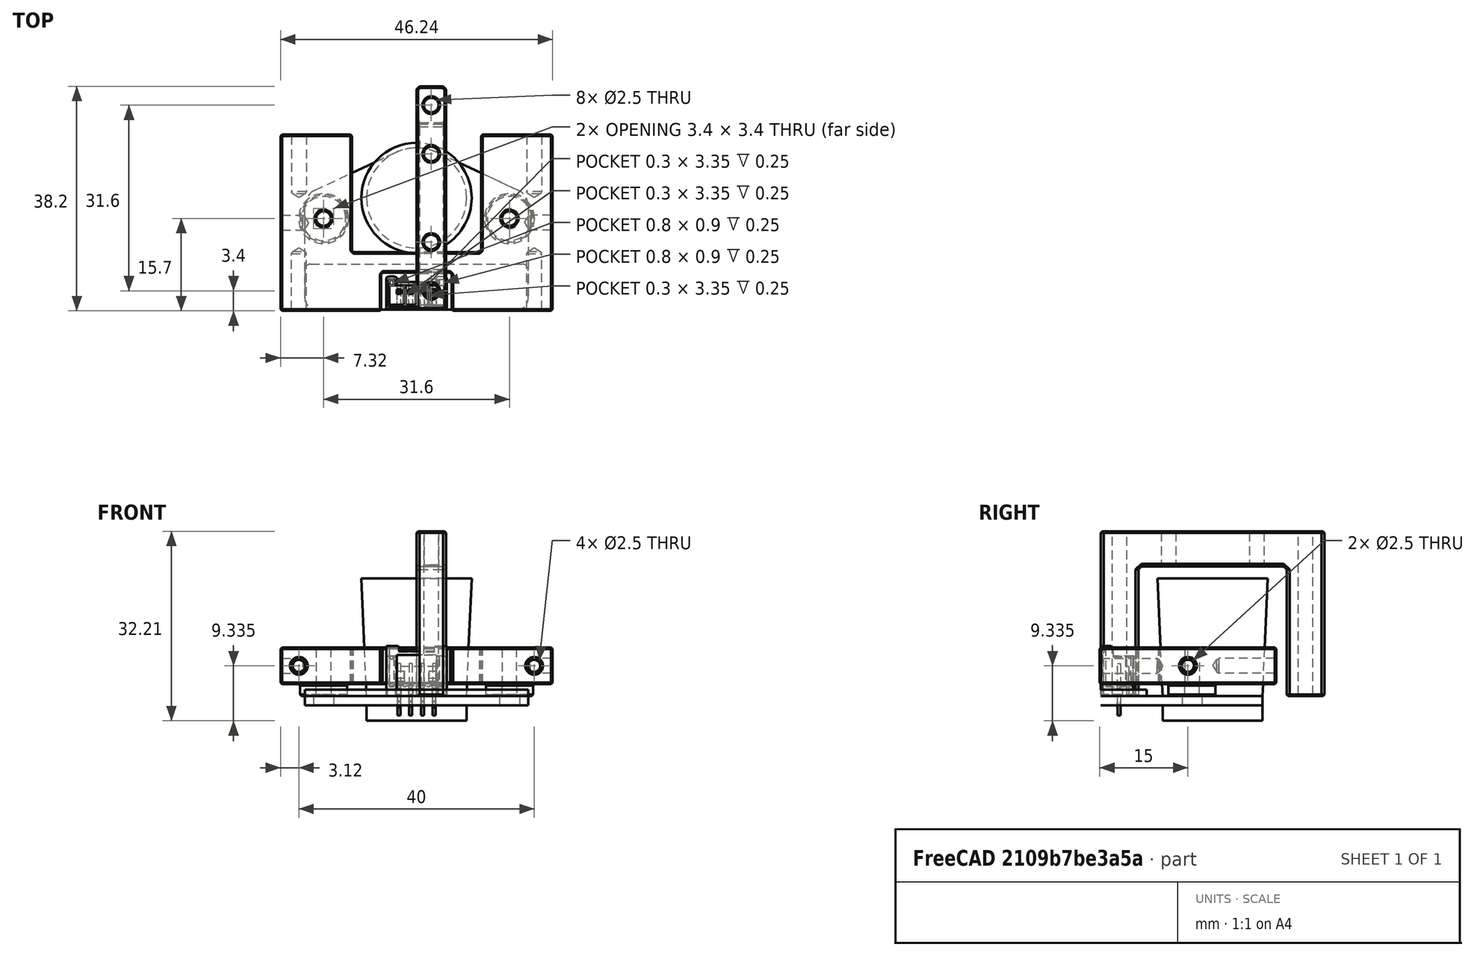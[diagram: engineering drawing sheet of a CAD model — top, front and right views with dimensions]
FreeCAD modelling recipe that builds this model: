
FCSTD DOCUMENT  (FreeCAD 0.21R33771 (Git))
Label: jubilee-beacon-mount
License: All rights reserved
LicenseURL: http://en.wikipedia.org/wiki/All_rights_reserved
objects: Sketcher::SketchObject×10, TechDraw::DrawViewDimension×8, PartDesign::Hole×7, TechDraw::DrawViewPart×6, Part::Feature×5, App::Part×4, PartDesign::Pad×3, PartDesign::Chamfer×3, PartDesign::Body×2, PartDesign::Pocket×1, TechDraw::DrawSVGTemplate×1, TechDraw::DrawPage×1
note: 53 computed .brp shape members not serialized (recipe doc carries the construction recipe); baked Part::Feature solids carry a one-line shape summary decoded from their .brp

FEATURE [Sketcher::SketchObject] Sketch
  FullyConstrained = true
  MapMode = 5
  Placement = pos=(0,0,0) rot=(0.57735,0.57735,0.57735;2.0944rad)
  Support = -> [YZ_Plane002]
  sketch-geometry (8):
    g0: LineSegment StartX=-19 StartY=0 StartZ=0 EndX=-19 EndY=28 EndZ=0
    g1: LineSegment StartX=-19 StartY=28 StartZ=0 EndX=19 EndY=28 EndZ=0
    g2: LineSegment StartX=19 StartY=28 StartZ=0 EndX=19 EndY=0 EndZ=0
    g3: LineSegment StartX=19 StartY=0 StartZ=0 EndX=12.6 EndY=0 EndZ=0
    g4: LineSegment StartX=12.6 StartY=0 StartZ=0 EndX=12.6 EndY=22 EndZ=0
    g5: LineSegment StartX=12.6 StartY=22 StartZ=0 EndX=-12.6 EndY=22 EndZ=0
    g6: LineSegment StartX=-12.6 StartY=22 StartZ=0 EndX=-12.6 EndY=0 EndZ=0
    g7: LineSegment StartX=-12.6 StartY=0 StartZ=0 EndX=-19 EndY=0 EndZ=0
  constraints (22):
    c: PointOnObject(g0,g-1)
    c: Vertical(g0)
    c: Coincident(g0,g1)
    c: Coincident(g1,g2)
    c: PointOnObject(g2,g-1)
    c: Vertical(g2)
    c: Coincident(g2,g3)
    c: PointOnObject(g3,g-1)
    c: Coincident(g3,g4)
    c: Vertical(g4)
    c: Coincident(g4,g5)
    c: Coincident(g5,g6)
    c: PointOnObject(g6,g-1)
    c: Vertical(g6)
    c: Coincident(g6,g7)
    c: Coincident(g7,g0)
    c: Symmetric(g5,g4,g-2)
    c: Symmetric(g0,g1,g-2)
    c: DistanceX(g0,g2) = 38
    c: DistanceX(g6,g3) = 25.2
    c: DistanceY(g2,g4) = 22
    c: DistanceY(g2,g1) = 28
FEATURE [PartDesign::Pad] Pad
  Direction = (1,-2e-16,3e-16)
  Length = 5
  Length2 = 10
  Placement = pos=(0,0,0) rot=(0.57735,0.57735,0.57735;2.0944rad)
  Profile = -> Sketch
  ReferenceAxis = -> Sketch [N_Axis]
  Type = 0
FEATURE [Sketcher::SketchObject] Sketch001
  FullyConstrained = true
  MapMode = 5
  Placement = pos=(0,0,1e-16) rot=(0.707107,0.707107,0;3.14159rad)
  Support = -> [Pad]
  sketch-geometry (2):
    g0: Circle CenterX=-15.8 CenterY=2.5 CenterZ=0 NormalX=0 NormalY=0 NormalZ=1 AngleXU=0 Radius=1.5
    g1: Circle CenterX=15.8 CenterY=2.5 CenterZ=0 NormalX=0 NormalY=0 NormalZ=1 AngleXU=0 Radius=1.5
  constraints (5):
    c: DistanceX(g0,g1) = 31.6
    c: Symmetric(g0,g1,g-2)
    c: DistanceY(g-1,g0) = 2.5
    c: Diameter(g0) = 3
    c: Equal(g0,g1)
FEATURE [PartDesign::Hole] Hole
  BaseFeature = -> Pad
  CustomThreadClearance = 0
  Depth = 95.8809
  DepthType = 1
  Diameter = 2.5
  DrillForDepth = false
  DrillPoint = 1
  DrillPointAngle = 118
  HoleCutCountersinkAngle = 90
  HoleCutCustomValues = false
  HoleCutDepth = 0
  HoleCutDiameter = 6.1
  HoleCutType = 0
  ModelThread = false
  Placement = pos=(0,0,0) rot=(0.57735,0.57735,0.57735;2.0944rad)
  Profile = -> Sketch001
  Tapered = false
  TaperedAngle = 90
  ThreadClass = 0
  ThreadDepth = 95.8809
  ThreadDepthType = 0
  ThreadDirection = 0
  ThreadFit = 0
  ThreadSize = 9
  ThreadType = 1
  Threaded = true
  UseCustomThreadClearance = false
FEATURE [Sketcher::SketchObject] Sketch002
  ExternalGeometry = -> [Hole]
  FullyConstrained = true
  MapMode = 5
  Placement = pos=(-7.8e-15,1.23e-14,28) rot=(0,0,-1;1.5708rad)
  Support = -> [Hole]
  sketch-geometry (3):
    g0: Circle CenterX=-7.5 CenterY=2.5 CenterZ=0 NormalX=0 NormalY=0 NormalZ=1 AngleXU=0 Radius=1.5
    g1: Circle CenterX=7.5 CenterY=2.5 CenterZ=0 NormalX=0 NormalY=0 NormalZ=1 AngleXU=0 Radius=1.5
    g2: GeomPoint X=-19 Y=2.5 Z=0
  constraints (6):
    c: DistanceX(g0,g1) = 15
    c: Symmetric(g1,g0,g-2)
    c: Diameter(g0) = 3
    c: Equal(g0,g1)
    c: Horizontal(g2,g0)
    c: Symmetric(g-3,g-3,g2)
FEATURE [PartDesign::Hole] Hole001
  BaseFeature = -> Hole
  CustomThreadClearance = 0
  Depth = 95.8809
  DepthType = 1
  Diameter = 2.5
  DrillForDepth = false
  DrillPoint = 1
  DrillPointAngle = 118
  HoleCutCountersinkAngle = 90
  HoleCutCustomValues = false
  HoleCutDepth = 0
  HoleCutDiameter = 6.1
  HoleCutType = 0
  ModelThread = false
  Placement = pos=(0,0,0) rot=(0.57735,0.57735,0.57735;2.0944rad)
  Profile = -> Sketch002
  Tapered = false
  TaperedAngle = 90
  ThreadClass = 0
  ThreadDepth = 95.8809
  ThreadDepthType = 0
  ThreadDirection = 0
  ThreadFit = 0
  ThreadSize = 9
  ThreadType = 1
  Threaded = true
  UseCustomThreadClearance = false
FEATURE [PartDesign::Chamfer] Chamfer
  Angle = 45
  Base = -> Hole001 [Edge18,Edge23,Edge19,Edge36,Edge24,Edge25,Edge26,Edge20,Edge3,Edge16,Edge21,Edge4]
  BaseFeature = -> Hole001
  ChamferType = 0
  FlipDirection = false
  Placement = pos=(0,0,0) rot=(0.57735,0.57735,0.57735;2.0944rad)
  Size = 0.5
  Size2 = 1
  SupportTransform = false
  UseAllEdges = false
FEATURE [PartDesign::Chamfer] Chamfer001
  Angle = 45
  Base = -> Chamfer [Edge9,Edge11,Edge1,Edge8,Edge10,Edge6,Edge5,Edge7,Edge40,Edge63,Edge64,Edge62,Edge34,Edge47,Edge50,Edge49,Edge12,Edge52,Edge22,Edge24,Edge25,Edge23,Edge18,Edge20,Edge21,Edge19,Edge17,Edge14,Edge4,Edge16,Edge54,Edge56]
  BaseFeature = -> Chamfer
  ChamferType = 0
  FlipDirection = false
  Placement = pos=(0,0,0) rot=(0.57735,0.57735,0.57735;2.0944rad)
  Size = 0.25
  Size2 = 1
  SupportTransform = false
  UseAllEdges = false
FEATURE [PartDesign::Body] Body  label="body"
  Group = -> [Sketch,Pad,Sketch001,Hole,Sketch002,Hole001,Chamfer,Chamfer001]
  Origin = -> Origin002
  Tip = -> Chamfer001
FEATURE [App::Part] Part  label="long-bracket"
  Group = -> [Body]
  Origin = -> Origin001
  Placement = pos=(-6,0,0) rot=(0,0,1;0rad)
FEATURE [Sketcher::SketchObject] Sketch003  label="horizontal-profile"
  FullyConstrained = true
  MapMode = 5
  Support = -> [XY_Plane004]
  sketch-geometry (10):
    g0: LineSegment StartX=23.125 StartY=10.8 StartZ=0 EndX=23.125 EndY=-19.2 EndZ=0
    g1: LineSegment StartX=23.125 StartY=-19.2 StartZ=0 EndX=-23.125 EndY=-19.2 EndZ=0
    g2: LineSegment StartX=-23.125 StartY=-19.2 StartZ=0 EndX=-23.125 EndY=10.8 EndZ=0
    g3: LineSegment StartX=-23.125 StartY=10.8 StartZ=0 EndX=-11 EndY=10.8 EndZ=0
    g4: LineSegment StartX=-11 StartY=10.8 StartZ=0 EndX=-11 EndY=-9.2 EndZ=0
    g5: LineSegment StartX=23.125 StartY=10.8 StartZ=0 EndX=11 EndY=10.8 EndZ=0
    g6: LineSegment StartX=11 StartY=10.8 StartZ=0 EndX=11 EndY=-9.2 EndZ=0
    g7: LineSegment StartX=11 StartY=-9.2 StartZ=0 EndX=-11 EndY=-9.2 EndZ=0
    g8: Circle CenterX=-15.8 CenterY=-3.5 CenterZ=0 NormalX=0 NormalY=0 NormalZ=1 AngleXU=0 Radius=1.25
    g9: Circle CenterX=15.8 CenterY=-3.5 CenterZ=0 NormalX=0 NormalY=0 NormalZ=1 AngleXU=0 Radius=1.25
  constraints (27):
    c: Coincident(g0,g1)
    c: Coincident(g1,g2)
    c: Horizontal(g1)
    c: Vertical(g0)
    c: DistanceY(g2,g2) = 30
    c: DistanceX(g2,g0) = 46.25
    c: Vertical(g2)
    c: Symmetric(g2,g0,g-2)
    c: Coincident(g2,g3)
    c: Horizontal(g3)
    c: Coincident(g3,g4)
    c: Vertical(g4)
    c: Coincident(g0,g5)
    c: Horizontal(g5)
    c: Coincident(g5,g6)
    c: Vertical(g6)
    c: Coincident(g6,g7)
    c: Coincident(g7,g4)
    c: Symmetric(g4,g6,g-2)
    c: DistanceX(g8,g9) = 31.6
    c: Diameter(g8) = 2.5
    c: Equal(g8,g9)
    c: Symmetric(g8,g9,g-2)
    c: DistanceY(g8,g-1) = 3.5
    c: DistanceY(g-1,g0) = 10.8
    c: DistanceX(g7,g7) = 22
    c: DistanceY(g6,g6) = 20
FEATURE [Part::Feature] Part__Feature  label="BeaconG_LP"
  shape: bbox 17 x 17 x 2.6 mm, 4 faces (baked)
FEATURE [Part::Feature] Part__Feature001  label="BeaconG_LP001"
  shape: bbox 18.75 x 18.75 x 20 mm, 4 faces (baked)
FEATURE [Part::Feature] Part__Feature002  label="BeaconG_LP002"
  shape: bbox 38 x 7.762 x 1.1 mm, 10 faces (baked)
FEATURE [Part::Feature] Part__Feature003  label="BeaconG_LP003"
  shape: bbox 38 x 27.5 x 1.611 mm, 18 faces (baked)
FEATURE [App::Part] BeaconG_LP  label="BeaconG_LP004"
  Group = -> [Part__Feature,Part__Feature001,Part__Feature002,Part__Feature003]
  Origin = -> Origin
FEATURE [Part::Feature] Part__Feature004  label="353620450"
  Placement = pos=(0,-16.1345,4.25) rot=(0,0.707107,0.707107;3.14159rad)
  shape: bbox 10.3 x 5.55 x 11.8 mm, 178 faces (baked)
FEATURE [App::Part] Beacon_Rev_H_Assm  label="Beacon Rev H Assm"
  Group = -> [BeaconG_LP,Part__Feature004]
  Origin = -> Origin005
FEATURE [PartDesign::Pad] Pad001  label="horizontal-base"
  Direction = (0,0,1)
  Length = 6.25
  Length2 = 10
  Profile = -> Sketch003
  ReferenceAxis = -> Sketch003 [N_Axis]
  Type = 0
FEATURE [Sketcher::SketchObject] Sketch004  label="mounting-studs-profile"
  ExternalGeometry = -> [Pad001]
  FullyConstrained = true
  MapMode = 5
  Placement = pos=(0,0,0) rot=(1,0,0;3.14159rad)
  Support = -> [Pad001]
  sketch-geometry (4):
    g0: Circle CenterX=15.8 CenterY=3.5 CenterZ=0 NormalX=0 NormalY=0 NormalZ=1 AngleXU=0 Radius=4
    g1: Circle CenterX=-15.8 CenterY=3.5 CenterZ=0 NormalX=0 NormalY=0 NormalZ=1 AngleXU=0 Radius=4
    g2: Circle CenterX=15.8 CenterY=3.5 CenterZ=0 NormalX=0 NormalY=0 NormalZ=1 AngleXU=0 Radius=1.25
    g3: Circle CenterX=-15.8 CenterY=3.5 CenterZ=0 NormalX=0 NormalY=0 NormalZ=1 AngleXU=0 Radius=1.25
  constraints (8):
    c: Coincident(g0,g-3)
    c: Coincident(g1,g-4)
    c: Equal(g0,g1)
    c: Diameter(g1) = 8
    c: Coincident(g2,g0)
    c: Equal(g2,g-3)
    c: Coincident(g3,g1)
    c: Equal(g3,g-4)
FEATURE [PartDesign::Pad] Pad002  label="mounting-studs"
  BaseFeature = -> Pad001
  Direction = (0,0,-1)
  Length = 2
  Length2 = 10
  Profile = -> Sketch004
  ReferenceAxis = -> Sketch004 [N_Axis]
  Type = 0
FEATURE [Sketcher::SketchObject] Sketch005  label="wire-cutout-profile"
  ExternalGeometry = -> [Pad002]
  FullyConstrained = true
  MapMode = 5
  Placement = pos=(0,0,6.25) rot=(0,0,1;0rad)
  Support = -> [Pad002]
  sketch-geometry (4):
    g0: LineSegment StartX=-6 StartY=-19.2 StartZ=0 EndX=6 EndY=-19.2 EndZ=0
    g1: LineSegment StartX=6 StartY=-19.2 StartZ=0 EndX=6 EndY=-12.7 EndZ=0
    g2: LineSegment StartX=6 StartY=-12.7 StartZ=0 EndX=-6 EndY=-12.7 EndZ=0
    g3: LineSegment StartX=-6 StartY=-12.7 StartZ=0 EndX=-6 EndY=-19.2 EndZ=0
  constraints (11):
    c: Coincident(g0,g1)
    c: Coincident(g1,g2)
    c: Coincident(g2,g3)
    c: Coincident(g3,g0)
    c: Horizontal(g2)
    c: Vertical(g1)
    c: Vertical(g3)
    c: PointOnObject(g0,g-3)
    c: Symmetric(g0,g0,g-2)
    c: DistanceX(g0,g0) = 12
    c: DistanceY(g1,g1) = 6.5
FEATURE [PartDesign::Pocket] Pocket  label="wire-cutout"
  BaseFeature = -> Pad002
  Direction = (0,0,-1)
  Length = 5
  Length2 = 5
  Profile = -> Sketch005
  ReferenceAxis = -> Sketch005 [N_Axis]
  Type = 1
FEATURE [Sketcher::SketchObject] Sketch006  label="joint-holes-rear-sketch"
  ExternalGeometry = -> [Pocket]
  FullyConstrained = true
  MapMode = 5
  Placement = pos=(0,10.8,0) rot=(0,0.707107,0.707107;3.14159rad)
  Support = -> [Pocket]
  sketch-geometry (3):
    g0: Circle CenterX=-20 CenterY=3.125 CenterZ=0 NormalX=0 NormalY=0 NormalZ=1 AngleXU=0 Radius=1.25
    g1: Circle CenterX=20 CenterY=3.125 CenterZ=0 NormalX=0 NormalY=0 NormalZ=1 AngleXU=0 Radius=1.25
    g2: GeomPoint X=-23.125 Y=3.125 Z=0
  constraints (6):
    c: Symmetric(g-3,g-3,g2)
    c: Horizontal(g2,g0)
    c: Symmetric(g0,g1,g-2)
    c: DistanceX(g0,g1) = 40
    c: Diameter(g0) = 2.5
    c: Equal(g0,g1)
FEATURE [Sketcher::SketchObject] Sketch007  label="joint-holes-front-sketch"
  ExternalGeometry = -> [Pocket]
  FullyConstrained = true
  MapMode = 5
  Placement = pos=(0,-19.2,0) rot=(1,0,0;1.5708rad)
  Support = -> [Pocket]
  sketch-geometry (3):
    g0: Circle CenterX=-20 CenterY=3.125 CenterZ=0 NormalX=0 NormalY=0 NormalZ=1 AngleXU=0 Radius=1.25
    g1: Circle CenterX=20 CenterY=3.125 CenterZ=0 NormalX=0 NormalY=0 NormalZ=1 AngleXU=0 Radius=1.25
    g2: GeomPoint X=-23.125 Y=3.125 Z=0
  constraints (6):
    c: Symmetric(g0,g1,g-2)
    c: Symmetric(g-3,g-3,g2)
    c: Horizontal(g0,g2)
    c: DistanceX(g0,g1) = 40
    c: Diameter(g0) = 2.5
    c: Equal(g0,g1)
FEATURE [Sketcher::SketchObject] Sketch008  label="joint-hole-right-sketch"
  ExternalGeometry = -> [Pocket]
  FullyConstrained = true
  MapMode = 5
  Placement = pos=(23.125,0,0) rot=(0.57735,0.57735,0.57735;2.0944rad)
  Support = -> [Pocket]
  sketch-geometry (3):
    g0: GeomPoint X=-4.2 Y=6.25 Z=0
    g1: GeomPoint X=-19.2 Y=3.125 Z=0
    g2: Circle CenterX=-4.2 CenterY=3.125 CenterZ=0 NormalX=0 NormalY=0 NormalZ=1 AngleXU=0 Radius=1.25
  constraints (5):
    c: Symmetric(g-3,g-4,g0)
    c: Symmetric(g-3,g-3,g1)
    c: Vertical(g2,g0)
    c: Horizontal(g1,g2)
    c: Diameter(g2) = 2.5
FEATURE [Sketcher::SketchObject] Sketch009  label="joint-hole-left-sketch"
  ExternalGeometry = -> [Pocket]
  FullyConstrained = true
  MapMode = 5
  Placement = pos=(-23.125,0,0) rot=(0.57735,-0.57735,-0.57735;2.0944rad)
  Support = -> [Pocket]
  sketch-geometry (3):
    g0: Circle CenterX=4.2 CenterY=3.125 CenterZ=0 NormalX=0 NormalY=0 NormalZ=1 AngleXU=0 Radius=1.25
    g1: GeomPoint X=4.2 Y=6.25 Z=0
    g2: GeomPoint X=-10.8 Y=3.125 Z=0
  constraints (5):
    c: Symmetric(g-3,g-4,g1)
    c: Symmetric(g-3,g-3,g2)
    c: Horizontal(g2,g0)
    c: Vertical(g0,g1)
    c: Diameter(g0) = 2.5
FEATURE [PartDesign::Hole] Hole002  label="joint-hole-left"
  BaseFeature = -> Pocket
  CustomThreadClearance = 0
  Depth = 4
  DepthType = 0
  Diameter = 2.5
  DrillForDepth = false
  DrillPoint = 1
  DrillPointAngle = 118
  HoleCutCountersinkAngle = 90
  HoleCutCustomValues = false
  HoleCutDepth = 0
  HoleCutDiameter = 6.1
  HoleCutType = 0
  ModelThread = false
  Profile = -> Sketch009
  Tapered = false
  TaperedAngle = 90
  ThreadClass = 0
  ThreadDepth = 4
  ThreadDepthType = 0
  ThreadDirection = 0
  ThreadFit = 0
  ThreadSize = 9
  ThreadType = 1
  Threaded = true
  UseCustomThreadClearance = false
FEATURE [PartDesign::Hole] Hole003  label="joint-hole-right"
  BaseFeature = -> Hole002
  CustomThreadClearance = 0
  Depth = 4
  DepthType = 0
  Diameter = 2.5
  DrillForDepth = false
  DrillPoint = 1
  DrillPointAngle = 118
  HoleCutCountersinkAngle = 90
  HoleCutCustomValues = false
  HoleCutDepth = 0
  HoleCutDiameter = 6.1
  HoleCutType = 0
  ModelThread = false
  Profile = -> Sketch008
  Tapered = false
  TaperedAngle = 90
  ThreadClass = 0
  ThreadDepth = 4
  ThreadDepthType = 0
  ThreadDirection = 0
  ThreadFit = 0
  ThreadSize = 9
  ThreadType = 1
  Threaded = true
  UseCustomThreadClearance = false
FEATURE [PartDesign::Hole] Hole004  label="joint-holes-rear"
  BaseFeature = -> Hole003
  CustomThreadClearance = 0
  Depth = 10
  DepthType = 0
  Diameter = 2.5
  DrillForDepth = false
  DrillPoint = 1
  DrillPointAngle = 118
  HoleCutCountersinkAngle = 90
  HoleCutCustomValues = false
  HoleCutDepth = 0
  HoleCutDiameter = 6.1
  HoleCutType = 0
  ModelThread = false
  Profile = -> Sketch006
  Tapered = false
  TaperedAngle = 90
  ThreadClass = 0
  ThreadDepth = 10
  ThreadDepthType = 0
  ThreadDirection = 0
  ThreadFit = 0
  ThreadSize = 9
  ThreadType = 1
  Threaded = true
  UseCustomThreadClearance = false
FEATURE [PartDesign::Hole] Hole005  label="joint-holes-front"
  BaseFeature = -> Hole004
  CustomThreadClearance = 0
  Depth = 10
  DepthType = 0
  Diameter = 2.5
  DrillForDepth = false
  DrillPoint = 1
  DrillPointAngle = 118
  HoleCutCountersinkAngle = 90
  HoleCutCustomValues = false
  HoleCutDepth = 0
  HoleCutDiameter = 6.1
  HoleCutType = 0
  ModelThread = false
  Profile = -> Sketch007
  Tapered = false
  TaperedAngle = 90
  ThreadClass = 0
  ThreadDepth = 10
  ThreadDepthType = 0
  ThreadDirection = 0
  ThreadFit = 0
  ThreadSize = 9
  ThreadType = 1
  Threaded = true
  UseCustomThreadClearance = false
FEATURE [TechDraw::DrawSVGTemplate] Template
  EditableTexts = Designed_by_Name=Designed by Name; Drawing_number=Drawing number; FC-Date=Date; FC-SC=Scale; FC-SH=Sheet; FC-Title=Title; Subtitle=Subtitle; Weight=Weight
  Height = 210
  Orientation = 1
  Template = <path>
  Width = 297
FEATURE [PartDesign::Hole] Hole006  label="mounting-holes"
  BaseFeature = -> Hole005
  CustomThreadClearance = 0
  Depth = 112.598
  DepthType = 1
  Diameter = 2.5
  DrillForDepth = false
  DrillPoint = 1
  DrillPointAngle = 118
  HoleCutCountersinkAngle = 90
  HoleCutCustomValues = false
  HoleCutDepth = 0
  HoleCutDiameter = 6.1
  HoleCutType = 0
  ModelThread = false
  Profile = -> Hole005 [Edge72,Edge71]
  Tapered = false
  TaperedAngle = 90
  ThreadClass = 0
  ThreadDepth = 112.598
  ThreadDepthType = 0
  ThreadDirection = 0
  ThreadFit = 0
  ThreadSize = 9
  ThreadType = 1
  Threaded = true
  UseCustomThreadClearance = false
FEATURE [PartDesign::Chamfer] Chamfer002  label="global-chamfer"
  Angle = 45
  Base = -> Hole006 [Edge72]
  BaseFeature = -> Hole006
  ChamferType = 0
  FlipDirection = false
  Size = 0.25
  Size2 = 1
  SupportTransform = false
  UseAllEdges = true
FEATURE [PartDesign::Body] Body001  label="bottom-plate"
  Group = -> [Sketch003,Pad001,Sketch004,Pad002,Sketch005,Pocket,Sketch006,Sketch007,Sketch008,Sketch009,Hole002,Hole003,Hole004,Hole005,Hole006,Chamfer002]
  Origin = -> Origin004
  Placement = pos=(0,0,2) rot=(0,0,1;0rad)
  Tip = -> Chamfer002
FEATURE [App::Part] Part001  label="direct-mount"
  Group = -> [Body001]
  Origin = -> Origin003
FEATURE [TechDraw::DrawViewPart] View  label="Front"
  CoarseView = false
  Direction = (0,-1,0)
  Focus = 100
  HardHidden = false
  IsoCount = 0
  IsoHidden = false
  IsoVisible = false
  LockPosition = false
  Perspective = false
  Rotation = 0
  ScaleType = 0
  ScrubCount = 0
  SeamHidden = false
  SeamVisible = false
  SmoothHidden = false
  SmoothVisible = true
  Source = -> [Body001]
  X = 167.591
  XDirection = (1,0,0)
  Y = 164.135
FEATURE [TechDraw::DrawViewPart] View001  label="Right"
  CoarseView = false
  Direction = (1,0,0)
  Focus = 100
  HardHidden = false
  IsoCount = 0
  IsoHidden = false
  IsoVisible = false
  LockPosition = false
  Perspective = false
  Rotation = 0
  ScaleType = 0
  ScrubCount = 0
  SeamHidden = false
  SeamVisible = false
  SmoothHidden = false
  SmoothVisible = true
  Source = -> [Body001]
  X = 223.001
  XDirection = (0,1,0)
  Y = 163.902
FEATURE [TechDraw::DrawViewPart] View002  label="Left"
  CoarseView = false
  Direction = (-1,0,0)
  Focus = 100
  HardHidden = false
  IsoCount = 0
  IsoHidden = false
  IsoVisible = false
  LockPosition = false
  Perspective = false
  Rotation = 0
  ScaleType = 0
  ScrubCount = 0
  SeamHidden = false
  SeamVisible = false
  SmoothHidden = false
  SmoothVisible = true
  Source = -> [Body001]
  X = 115.906
  XDirection = (0,-1,0)
  Y = 163.902
FEATURE [TechDraw::DrawViewPart] View003  label="Rear"
  CoarseView = false
  Direction = (0,1,0)
  Focus = 100
  HardHidden = false
  IsoCount = 0
  IsoHidden = false
  IsoVisible = false
  LockPosition = false
  Perspective = false
  Rotation = 0
  ScaleType = 0
  ScrubCount = 0
  SeamHidden = false
  SeamVisible = false
  SmoothHidden = false
  SmoothVisible = true
  Source = -> [Body001]
  X = 166.516
  XDirection = (-1,0,0)
  Y = 73.6419
FEATURE [TechDraw::DrawViewPart] View005  label="Isometric"
  CoarseView = false
  Direction = (0.57735,-0.57735,0.57735)
  Focus = 100
  HardHidden = false
  IsoCount = 0
  IsoHidden = false
  IsoVisible = false
  LockPosition = false
  Perspective = false
  Rotation = 0
  ScaleType = 0
  ScrubCount = 0
  SeamHidden = false
  SeamVisible = false
  SmoothHidden = false
  SmoothVisible = true
  Source = -> [Body001]
  X = 54.2095
  XDirection = (0.707107,0.707107,0)
  Y = 169.257
FEATURE [TechDraw::DrawViewDimension] Dimension
  AngleOverride = false
  Arbitrary = true
  ArbitraryTolerances = false
  EqualTolerance = true
  ExtensionAngle = 0
  FormatSpec = M3 G4
  FormatSpecOverTolerance = %+.2w
  FormatSpecUnderTolerance = %+.2w
  Inverted = false
  LineAngle = 0
  LockPosition = false
  MeasureType = 1
  OverTolerance = 0
  References2D = -> [View002]
  Rotation = 0
  ScaleType = 0
  TheoreticalExact = false
  Type = 5
  UnderTolerance = 0
  X = 15.2424
  Y = 17.6115
FEATURE [TechDraw::DrawViewDimension] Dimension001
  AngleOverride = false
  Arbitrary = true
  ArbitraryTolerances = false
  EqualTolerance = true
  ExtensionAngle = 0
  FormatSpec = M3 G4
  FormatSpecOverTolerance = %+.2w
  FormatSpecUnderTolerance = %+.2w
  Inverted = false
  LineAngle = 0
  LockPosition = false
  MeasureType = 1
  OverTolerance = 0
  References2D = -> [View]
  Rotation = 0
  ScaleType = 0
  TheoreticalExact = false
  Type = 5
  UnderTolerance = 0
  X = -4.37251
  Y = 17.3366
FEATURE [TechDraw::DrawViewDimension] Dimension002
  AngleOverride = false
  Arbitrary = true
  ArbitraryTolerances = false
  EqualTolerance = true
  ExtensionAngle = 0
  FormatSpec = M3 G4
  FormatSpecOverTolerance = %+.2w
  FormatSpecUnderTolerance = %+.2w
  Inverted = false
  LineAngle = 0
  LockPosition = false
  MeasureType = 1
  OverTolerance = 0
  References2D = -> [View]
  Rotation = 0
  ScaleType = 0
  TheoreticalExact = false
  Type = 5
  UnderTolerance = 0
  X = 35.1706
  Y = 17.1363
FEATURE [TechDraw::DrawViewDimension] Dimension003
  AngleOverride = false
  Arbitrary = true
  ArbitraryTolerances = false
  EqualTolerance = true
  ExtensionAngle = 0
  FormatSpec = M3 G4
  FormatSpecOverTolerance = %+.2w
  FormatSpecUnderTolerance = %+.2w
  Inverted = false
  LineAngle = 0
  LockPosition = false
  MeasureType = 1
  OverTolerance = 0
  References2D = -> [View001]
  Rotation = 0
  ScaleType = 0
  TheoreticalExact = false
  Type = 5
  UnderTolerance = 0
  X = 18.9104
  Y = 17.4407
FEATURE [TechDraw::DrawViewPart] View006  label="Bottom"
  CoarseView = false
  Direction = (0,0,-1)
  Focus = 100
  HardHidden = false
  IsoCount = 0
  IsoHidden = false
  IsoVisible = false
  LockPosition = false
  Perspective = false
  Rotation = 0
  ScaleType = 0
  ScrubCount = 0
  SeamHidden = false
  SeamVisible = false
  SmoothHidden = false
  SmoothVisible = true
  Source = -> [Body001]
  X = 168.183
  XDirection = (1,0,0)
  Y = 120.668
FEATURE [TechDraw::DrawViewDimension] Dimension004
  AngleOverride = false
  Arbitrary = true
  ArbitraryTolerances = false
  EqualTolerance = true
  ExtensionAngle = 0
  FormatSpec = M3 G4
  FormatSpecOverTolerance = %+.2w
  FormatSpecUnderTolerance = %+.2w
  Inverted = false
  LineAngle = 0
  LockPosition = false
  MeasureType = 1
  OverTolerance = 0
  References2D = -> [View006]
  Rotation = 0
  ScaleType = 0
  TheoreticalExact = false
  Type = 5
  UnderTolerance = 0
  X = 33.9405
  Y = 24.7444
FEATURE [TechDraw::DrawViewDimension] Dimension005
  AngleOverride = false
  Arbitrary = true
  ArbitraryTolerances = false
  EqualTolerance = true
  ExtensionAngle = 0
  FormatSpec = M3 G4
  FormatSpecOverTolerance = %+.2w
  FormatSpecUnderTolerance = %+.2w
  Inverted = false
  LineAngle = 0
  LockPosition = false
  MeasureType = 1
  OverTolerance = 0
  References2D = -> [View006]
  Rotation = 0
  ScaleType = 0
  TheoreticalExact = false
  Type = 5
  UnderTolerance = 0
  X = 5.18967
  Y = 24.8382
FEATURE [TechDraw::DrawViewDimension] Dimension006
  AngleOverride = false
  Arbitrary = true
  ArbitraryTolerances = false
  EqualTolerance = true
  ExtensionAngle = 0
  FormatSpec = M3 G4
  FormatSpecOverTolerance = %+.2w
  FormatSpecUnderTolerance = %+.2w
  Inverted = false
  LineAngle = 0
  LockPosition = false
  MeasureType = 1
  OverTolerance = 0
  References2D = -> [View003]
  Rotation = 0
  ScaleType = 0
  TheoreticalExact = false
  Type = 5
  UnderTolerance = 0
  X = 1.46873
  Y = 18.7437
FEATURE [TechDraw::DrawViewDimension] Dimension007
  AngleOverride = false
  Arbitrary = true
  ArbitraryTolerances = false
  EqualTolerance = true
  ExtensionAngle = 0
  FormatSpec = M3 G4
  FormatSpecOverTolerance = %+.2w
  FormatSpecUnderTolerance = %+.2w
  Inverted = false
  LineAngle = 0
  LockPosition = false
  MeasureType = 1
  OverTolerance = 0
  References2D = -> [View003]
  Rotation = 0
  ScaleType = 0
  TheoreticalExact = false
  Type = 5
  UnderTolerance = 0
  X = 37.8371
  Y = 17.9744
FEATURE [TechDraw::DrawPage] Page  label="threads"
  KeepUpdated = true
  NextBalloonIndex = 1
  ProjectionType = 0
  Template = -> Template
  Views = -> [View,View001,View002,View003,View005,Dimension,Dimension001,Dimension002,Dimension003,View006,Dimension004,Dimension005,Dimension006,Dimension007]
note: 1 file-system path scrubbed to <path> (originals preserved in the JSON sidecar)
